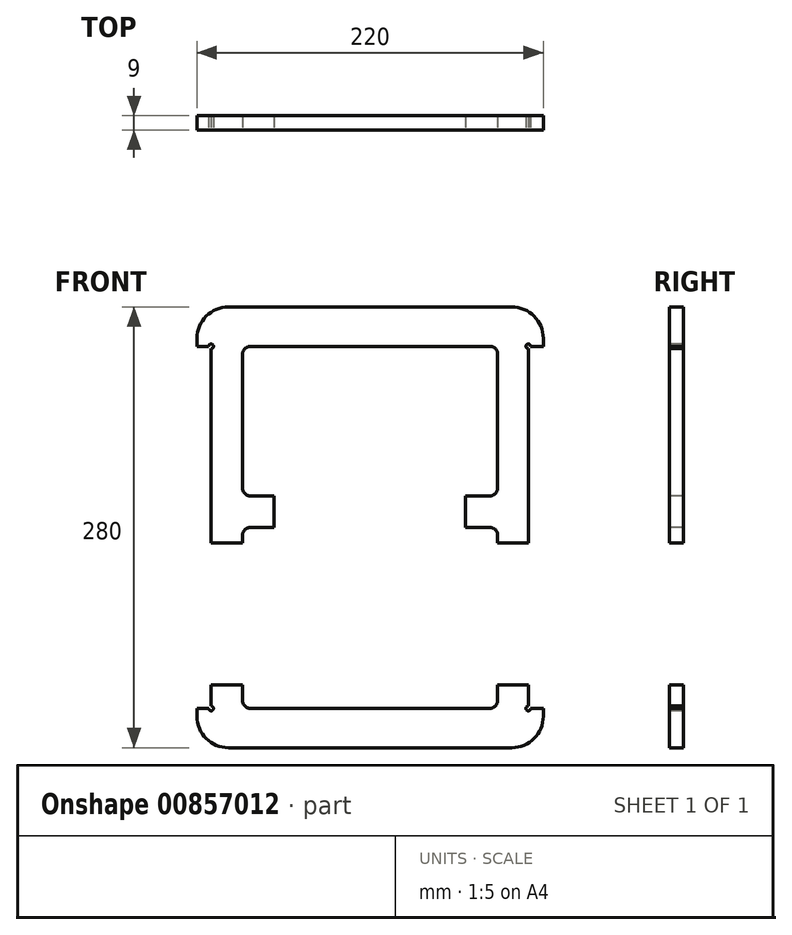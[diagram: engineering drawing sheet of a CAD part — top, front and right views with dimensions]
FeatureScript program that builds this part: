
annotation { "Feature Type Name" : "Feature", "Feature Type Description" : "" }
export const myFeature = defineFeature(function(context is Context, id is Id, definition is map)
    precondition{}
    {
        {
            var Q0;
            Q0=qCreatedBy(makeId("Front.planeOp"),FACE);
            var sketch = newSketch(context, id + "F0", { "sketchPlane" : qUnion([Q0])});
            skLineSegment(sketch, "E0.bottom", {"start": v(-90, 137.55) * mm, "end": v(90, 137.55) * mm});
            skLineSegment(sketch, "E0.top", {"start": v(-90, -142.45) * mm, "end": v(90, -142.45) * mm});
            skLineSegment(sketch, "E0.left", {"start": v(-110, 117.55) * mm, "end": v(-110, 112.55) * mm});
            skLineSegment(sketch, "E0.right", {"start": v(110, 117.55) * mm, "end": v(110, 112.55) * mm});
            skPoint(sketch, "E0.middle", {"position": v(0, -2.45) * mm});
            skLineSegment(sketch, "E1.bottom", {"start": v(-76, 17.55) * mm, "end": v(-61, 17.55) * mm});
            skLineSegment(sketch, "E2", {"start": v(-110, 112.55) * mm, "end": v(-101, 112.55) * mm});
            skLineSegment(sketch, "E3", {"start": v(-110, -117.45) * mm, "end": v(-101, -117.45) * mm});
            skLineSegment(sketch, "E4.0", {"start": v(-101, 112.55) * mm, "end": v(-101, -12.45) * mm});
            skLineSegment(sketch, "E5.trimOffspring", {"start": v(-110, -117.45) * mm, "end": v(-110, -122.45) * mm});
            skLineSegment(sketch, "E6.0", {"start": v(-81, 107.55) * mm, "end": v(-81, 22.55) * mm});
            skLineSegment(sketch, "E7.0", {"start": v(81, 107.55) * mm, "end": v(81, 22.55) * mm});
            skLineSegment(sketch, "E8.trimOffspring", {"start": v(-76, 112.55) * mm, "end": v(76, 112.55) * mm});
            skLineSegment(sketch, "E9.trimOffspring", {"start": v(-81, -7.45) * mm, "end": v(-81, -12.45) * mm});
            skLineSegment(sketch, "E10.trimOffspring", {"start": v(-76, -117.45) * mm, "end": v(76, -117.45) * mm});
            skLineSegment(sketch, "E11.trimOffspring", {"start": v(-76, -2.45) * mm, "end": v(-61, -2.45) * mm});
            skPoint(sketch, "E12.visualSharp", {"position": v(-110, 137.55) * mm});
            skArc(sketch, "E12.filletArc", {"start": v(-90, 137.55) * mm, "mid": v(-104.14, 131.7) * mm, "end": v(-110, 117.55) * mm});
            skPoint(sketch, "E13.visualSharp", {"position": v(110, 137.55) * mm});
            skArc(sketch, "E13.filletArc", {"start": v(110, 117.55) * mm, "mid": v(104.14, 131.7) * mm, "end": v(90, 137.55) * mm});
            skPoint(sketch, "E14.visualSharp", {"position": v(110, -142.45) * mm});
            skArc(sketch, "E14.filletArc", {"start": v(90, -142.45) * mm, "mid": v(104.14, -136.6) * mm, "end": v(110, -122.45) * mm});
            skPoint(sketch, "E15.visualSharp", {"position": v(-110, -142.45) * mm});
            skArc(sketch, "E15.filletArc", {"start": v(-110, -122.45) * mm, "mid": v(-104.14, -136.6) * mm, "end": v(-90, -142.45) * mm});
            skLineSegment(sketch, "E16.trimOffspring", {"start": v(110, -117.45) * mm, "end": v(110, -122.45) * mm});
            skLineSegment(sketch, "E17.trimOffspring", {"start": v(100.5, -117.45) * mm, "end": v(110, -117.45) * mm});
            skLineSegment(sketch, "E18.trimOffspring", {"start": v(81, -7.45) * mm, "end": v(81, -112.45) * mm});
            skLineSegment(sketch, "E19.trimOffspring", {"start": v(100.5, 112.55) * mm, "end": v(100.5, -117.45) * mm});
            skLineSegment(sketch, "E20.trimOffspring", {"start": v(100.5, 112.55) * mm, "end": v(110, 112.55) * mm});
            skPoint(sketch, "E21.visualSharp", {"position": v(81, 17.55) * mm});
            skArc(sketch, "E21.filletArc", {"start": v(76, 17.55) * mm, "mid": v(79.54, 19.02) * mm, "end": v(81, 22.55) * mm});
            skPoint(sketch, "E22.visualSharp", {"position": v(-81, 17.55) * mm});
            skArc(sketch, "E22.filletArc", {"start": v(-81, 22.55) * mm, "mid": v(-79.54, 19.02) * mm, "end": v(-76, 17.55) * mm});
            skPoint(sketch, "E23.visualSharp", {"position": v(-81, -2.45) * mm});
            skArc(sketch, "E23.filletArc", {"start": v(-76, -2.45) * mm, "mid": v(-79.54, -3.91) * mm, "end": v(-81, -7.45) * mm});
            skPoint(sketch, "E24.visualSharp", {"position": v(81, -2.45) * mm});
            skArc(sketch, "E24.filletArc", {"start": v(81, -7.45) * mm, "mid": v(79.54, -3.91) * mm, "end": v(76, -2.45) * mm});
            skPoint(sketch, "E25.visualSharp", {"position": v(81, -117.45) * mm});
            skArc(sketch, "E25.filletArc", {"start": v(76, -117.45) * mm, "mid": v(79.54, -115.98) * mm, "end": v(81, -112.45) * mm});
            skPoint(sketch, "E26.visualSharp", {"position": v(-81, -117.45) * mm});
            skArc(sketch, "E26.filletArc", {"start": v(-81, -112.45) * mm, "mid": v(-79.54, -115.98) * mm, "end": v(-76, -117.45) * mm});
            skPoint(sketch, "E27.visualSharp", {"position": v(-81, 112.55) * mm});
            skArc(sketch, "E27.filletArc", {"start": v(-76, 112.55) * mm, "mid": v(-79.54, 111.09) * mm, "end": v(-81, 107.55) * mm});
            skPoint(sketch, "E28.visualSharp", {"position": v(81, 112.55) * mm});
            skArc(sketch, "E28.filletArc", {"start": v(81, 107.55) * mm, "mid": v(79.54, 111.09) * mm, "end": v(76, 112.55) * mm});
            skCircle(sketch, "E29", {"center": v(-101, 112.55) * mm, "radius": 1.5 * mm});
            skCircle(sketch, "E30", {"center": v(100.5, 112.55) * mm, "radius": 1.5 * mm});
            skCircle(sketch, "E31", {"center": v(-101, -117.45) * mm, "radius": 1.5 * mm});
            skCircle(sketch, "E32", {"center": v(100.5, -117.45) * mm, "radius": 1.5 * mm});
            skLineSegment(sketch, "E33.bottom", {"start": v(-101, -12.45) * mm, "end": v(-81, -12.45) * mm});
            skLineSegment(sketch, "E33.top", {"start": v(-101, -102.45) * mm, "end": v(-81, -102.45) * mm});
            skLineSegment(sketch, "E33.right", {"start": v(100.5, -12.45) * mm, "end": v(100.5, -102.45) * mm});
            skLineSegment(sketch, "E34.trimOffspring", {"start": v(-81, -102.45) * mm, "end": v(-81, -112.45) * mm});
            skLineSegment(sketch, "E35.trimOffspring", {"start": v(81, -102.45) * mm, "end": v(100.5, -102.45) * mm});
            skLineSegment(sketch, "E36.trimOffspring", {"start": v(81, -12.45) * mm, "end": v(100.5, -12.45) * mm});
            skLineSegment(sketch, "E37.trimOffspring", {"start": v(-101, -102.45) * mm, "end": v(-101, -117.45) * mm});
            skLineSegment(sketch, "E38.left", {"start": v(-61, 17.55) * mm, "end": v(-61, -2.45) * mm});
            skLineSegment(sketch, "E38.right", {"start": v(60.5, 17.55) * mm, "end": v(60.5, -2.45) * mm});
            skLineSegment(sketch, "E39.trimOffspring", {"start": v(60.5, 17.55) * mm, "end": v(76, 17.55) * mm});
            skLineSegment(sketch, "E40.trimOffspring", {"start": v(60.5, -2.45) * mm, "end": v(76, -2.45) * mm});
            skSolve(sketch);
        }
        {
            var Q0;
            Q0=makeQuery(id+"F0.imprint","IMPRINT",FACE,{"disambiguationData":[TD([[makeQuery(id+"F0.imprint","IMPRINT",EDGE,{"derivedFrom":sQuery(id+"F0.wireOp",EDGE,"E0.top")}),1.0]])]});
            var Q1;
            Q1=makeQuery(id+"F0.imprint","IMPRINT",FACE,{"disambiguationData":[TD([[makeQuery(id+"F0.imprint","IMPRINT",EDGE,{"derivedFrom":sQuery(id+"F0.wireOp",EDGE,"E33.right")}),-1.0]])]});
            var Q2;
            Q2=makeQuery(id+"F0.imprint","IMPRINT",FACE,{"disambiguationData":[TD([[makeQuery(id+"F0.imprint","IMPRINT",EDGE,{"derivedFrom":sQuery(id+"F0.wireOp",EDGE,"E0.bottom")}),-1.0]])]});
            extrude(context, id + "F1", {"entities" : qUnion([Q0, Q1, Q2]), "oppositeDirection" : true, "depth" : 9 * mm, "offsetDistance" : 25 * mm});
        }
    });
